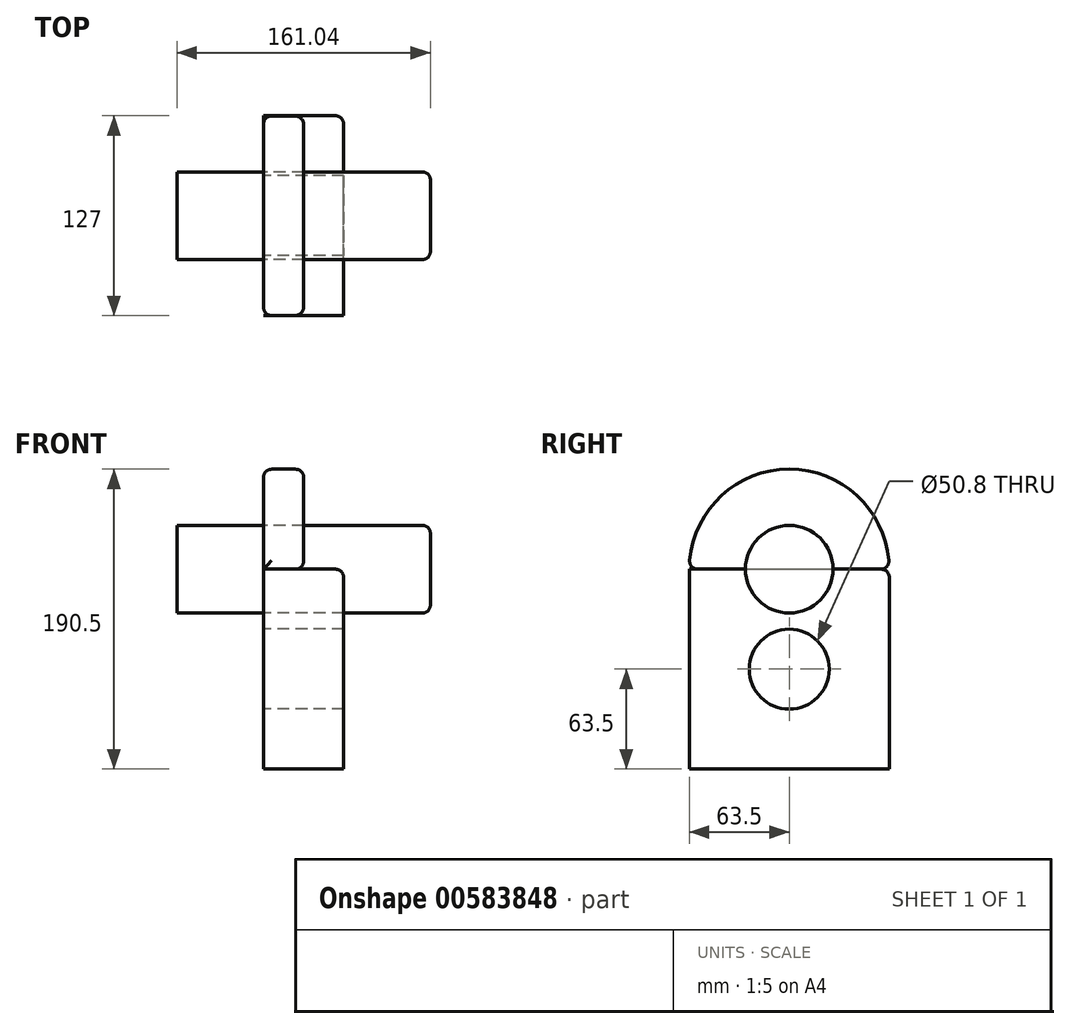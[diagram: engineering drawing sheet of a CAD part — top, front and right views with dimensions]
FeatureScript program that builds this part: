
annotation { "Feature Type Name" : "Feature", "Feature Type Description" : "" }
export const myFeature = defineFeature(function(context is Context, id is Id, definition is map)
    precondition{}
    {
        {
            var Q0;
            Q0=qCreatedBy(makeId("Right.planeOp"),FACE);
            var sketch = newSketch(context, id + "F0", { "sketchPlane" : qUnion([Q0])});
            skLineSegment(sketch, "E0.bottom", {"start": v(-63.5, -63.5) * mm, "end": v(63.5, -63.5) * mm});
            skLineSegment(sketch, "E0.top", {"start": v(-63.5, 63.5) * mm, "end": v(63.5, 63.5) * mm});
            skLineSegment(sketch, "E0.left", {"start": v(-63.5, -63.5) * mm, "end": v(-63.5, 63.5) * mm});
            skLineSegment(sketch, "E0.right", {"start": v(63.5, -63.5) * mm, "end": v(63.5, 63.5) * mm});
            skPoint(sketch, "E0.middle", {"position": v(0, 0) * mm});
            skCircle(sketch, "E1", {"center": v(0, 0) * mm, "radius": 25.4 * mm});
            skSolve(sketch);
        }
        {
            var Q0;
            Q0 = qSketchRegion(id + "F0", true);
            extrude(context, id + "F1", {"entities" : qUnion([Q0]), "endBound" : BoundingType.SYMMETRIC, "depth" : 50.8 * mm, "offsetDistance" : 25.4 * mm});
        }
        {
            var Q0;
            Q0=makeQuery(id+"F1.opExtrude","CAP_FACE",FACE,{"disambiguationData":[OSD([sQuery(id+"F0.wireOp",EDGE,"E0.bottom"),sQuery(id+"F0.wireOp",EDGE,"E0.top"),sQuery(id+"F0.wireOp",EDGE,"E0.left"),sQuery(id+"F0.wireOp",EDGE,"E0.right"),sQuery(id+"F0.wireOp",EDGE,"E1")])],"isStart":true});
            var sketch = newSketch(context, id + "F2", { "sketchPlane" : qUnion([Q0])});
            skArc(sketch, "E2", {"start": v(63.5, 63.5) * mm, "mid": v(0, 127) * mm, "end": v(-63.5, 63.5) * mm});
            skArc(sketch, "E3", {"start": v(45.08, 63.5) * mm, "mid": v(0, 108.58) * mm, "end": v(-45.08, 63.5) * mm});
            skLineSegment(sketch, "E4", {"start": v(-63.5, 63.5) * mm, "end": v(63.5, 63.5) * mm});
            skSolve(sketch);
        }
        {
            var Q0;
            Q0 = qSketchRegion(id + "F2", true);
            extrude(context, id + "F3", {"entities" : qUnion([Q0]), "oppositeDirection" : true, "depth" : 25.4 * mm, "offsetDistance" : 25.4 * mm});
        }
        {
            var Q0;
            Q0=makeQuery(id+"F3.opExtrude","CAP_FACE",FACE,{"disambiguationData":[OSD([sQuery(id+"F2.wireOp",EDGE,"E2"),sQuery(id+"F2.wireOp",EDGE,"E4")])],"isStart":false});
            var sketch = newSketch(context, id + "F4", { "sketchPlane" : qUnion([Q0])});
            skCircle(sketch, "E5", {"center": v(0, 63.5) * mm, "radius": 27.83 * mm});
            skSolve(sketch);
        }
        {
            var Q0;
            Q0 = qSketchRegion(id + "F4", true);
            extrude(context, id + "F5", {"entities" : qUnion([Q0]), "endBound" : BoundingType.SYMMETRIC, "depth" : 161.04 * mm, "offsetDistance" : 25.4 * mm});
        }
        {
            var Q0;
            Q0=makeQuery(id+"F5.opExtrude","CAP_EDGE",EDGE,{"disambiguationData":[OSD([sQuery(id+"F4.wireOp",EDGE,"E5")])],"isStart":false});
            fillet(context, id + "F6", {"entities" : qUnion([Q0]), "radius" : 5.08 * mm, "tangentPropagation" : true, "allowEdgeOverflow" : false});
        }
        {
            var Q0;
            Q0=makeQuery(id+"F3.opExtrude","CAP_EDGE",EDGE,{"disambiguationData":[OSD([sQuery(id+"F2.wireOp",EDGE,"E4")])],"isStart":false});
            var Q1;
            Q1=makeQuery(id+"F1.opExtrude","CAP_EDGE",EDGE,{"disambiguationData":[OSD([sQuery(id+"F0.wireOp",EDGE,"E0.top")])],"isStart":false});
            fillet(context, id + "F7", {"entities" : qUnion([Q0, Q1]), "radius" : 5.08 * mm, "tangentPropagation" : true, "allowEdgeOverflow" : false});
        }
        {
            var Q0;
            Q0=makeQuery(id+"F1.opExtrude","SWEPT_EDGE",EDGE,{"disambiguationData":[OSD([sQuery(id+"F0.wireOp",EDGE,"E0.top"),sQuery(id+"F0.wireOp",EDGE,"E0.right")])]});
            var Q1;
            Q1=makeQuery(id+"F7.opFillet","BLEND_EDGE",EDGE,{"blendedFrom":[makeQuery(id+"F1.opExtrude","CAP_EDGE",EDGE,{"disambiguationData":[OSD([sQuery(id+"F0.wireOp",EDGE,"E0.top")])],"isStart":false}),makeQuery(id+"F1.opExtrude","SWEPT_FACE",FACE,{"disambiguationData":[OSD([sQuery(id+"F0.wireOp",EDGE,"E0.right")])]})],"blendedInto":[makeQuery(id+"F1.opExtrude","SWEPT_FACE",FACE,{"disambiguationData":[OSD([sQuery(id+"F0.wireOp",EDGE,"E0.right")])]})]});
            var Q2;
            Q2=makeQuery(id+"F3.opExtrude","CAP_EDGE",EDGE,{"disambiguationData":[OSD([sQuery(id+"F2.wireOp",EDGE,"E2")])],"isStart":false});
            var Q3;
            Q3=makeQuery(id+"F3.opExtrude","CAP_EDGE",EDGE,{"disambiguationData":[OSD([sQuery(id+"F2.wireOp",EDGE,"E2")])],"isStart":true});
            fillet(context, id + "F8", {"entities" : qUnion([Q0, Q1, Q2, Q3]), "radius" : 5.08 * mm, "tangentPropagation" : true, "allowEdgeOverflow" : false});
        }
    });
